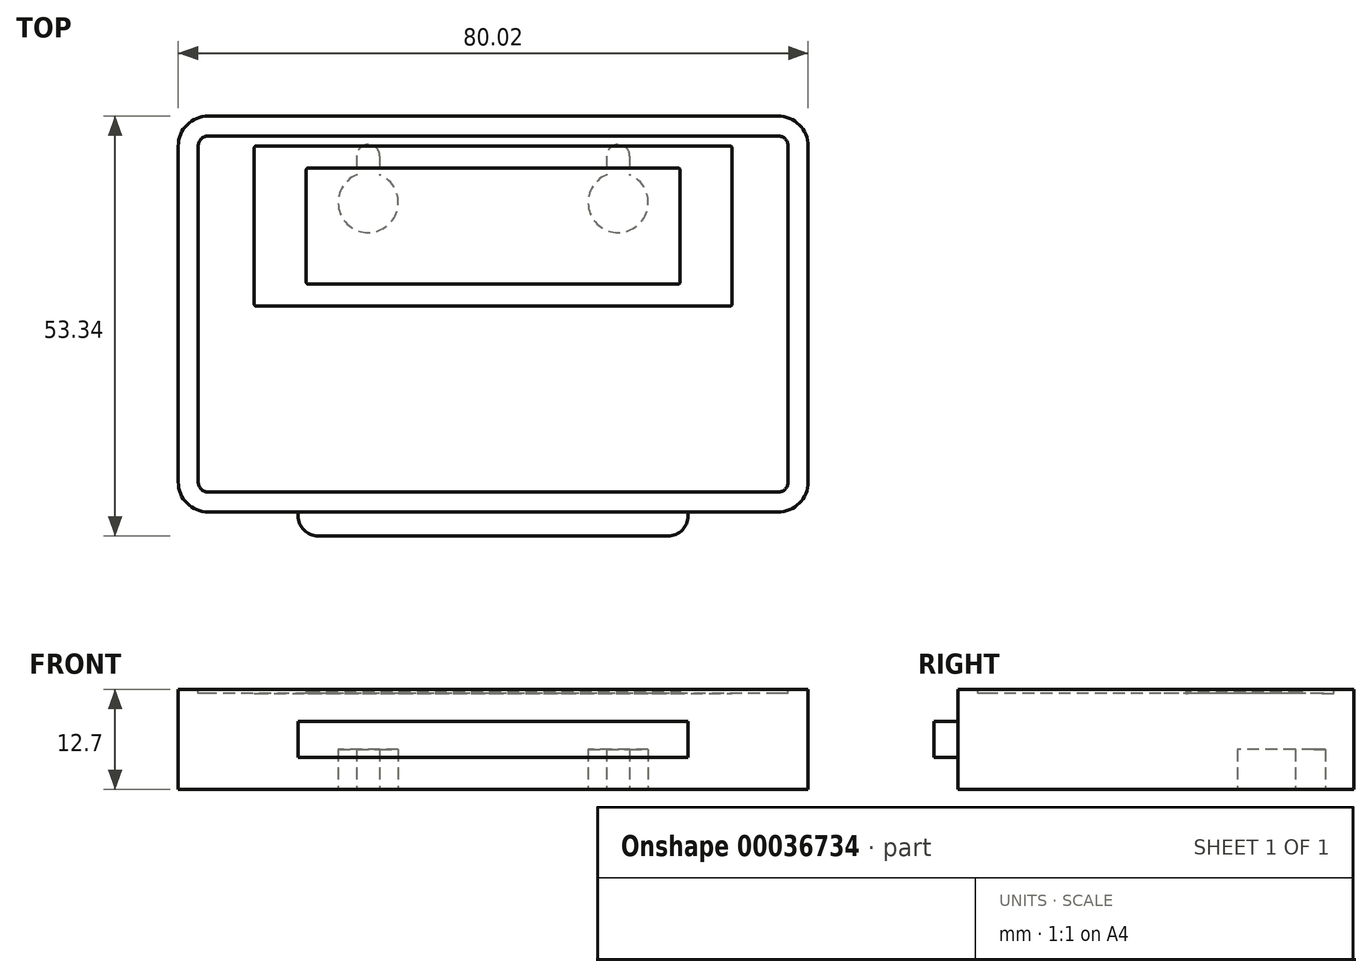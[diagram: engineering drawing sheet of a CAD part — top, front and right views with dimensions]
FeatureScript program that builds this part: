
annotation { "Feature Type Name" : "Feature", "Feature Type Description" : "" }
export const myFeature = defineFeature(function(context is Context, id is Id, definition is map)
    precondition{}
    {
        {
            var Q0;
            Q0=qCreatedBy(makeId("Top.planeOp"),FACE);
            var sketch = newSketch(context, id + "F0", { "sketchPlane" : qUnion([Q0])});
            skLineSegment(sketch, "E0.rect.bottom", {"start": v(40, 25.15) * mm, "end": v(-40, 25.15) * mm});
            skLineSegment(sketch, "E0.rect.top", {"start": v(40, -25.15) * mm, "end": v(-40, -25.15) * mm});
            skLineSegment(sketch, "E0.rect.left", {"start": v(40, 25.15) * mm, "end": v(40, -25.15) * mm});
            skLineSegment(sketch, "E0.rect.right", {"start": v(-40, 25.15) * mm, "end": v(-40, -25.15) * mm});
            skPoint(sketch, "E0.rect.middle", {"position": v(0, 0) * mm});
            skSolve(sketch);
        }
        {
            var Q0;
            Q0=makeQuery(id+"F0.imprint","IMPRINT",FACE,{"disambiguationData":[TD([[makeQuery(id+"F0.imprint","IMPRINT",EDGE,{"derivedFrom":sQuery(id+"F0.wireOp",EDGE,"E0.rect.bottom")}),1.0]])]});
            extrude(context, id + "F1", {"entities" : qUnion([Q0]), "endBound" : BoundingType.SYMMETRIC, "depth" : 12.7 * mm});
        }
        {
            var Q0;
            Q0=makeQuery(id+"F1.opExtrude","SWEPT_EDGE",EDGE,{"disambiguationData":[OSD([sQuery(id+"F0.wireOp",EDGE,"E0.rect.top"),sQuery(id+"F0.wireOp",EDGE,"E0.rect.right")])]});
            var Q1;
            Q1=makeQuery(id+"F1.opExtrude","SWEPT_EDGE",EDGE,{"disambiguationData":[OSD([sQuery(id+"F0.wireOp",EDGE,"E0.rect.top"),sQuery(id+"F0.wireOp",EDGE,"E0.rect.left")])]});
            var Q2;
            Q2=makeQuery(id+"F1.opExtrude","SWEPT_EDGE",EDGE,{"disambiguationData":[OSD([sQuery(id+"F0.wireOp",EDGE,"E0.rect.bottom"),sQuery(id+"F0.wireOp",EDGE,"E0.rect.left")])]});
            var Q3;
            Q3=makeQuery(id+"F1.opExtrude","SWEPT_EDGE",EDGE,{"disambiguationData":[OSD([sQuery(id+"F0.wireOp",EDGE,"E0.rect.bottom"),sQuery(id+"F0.wireOp",EDGE,"E0.rect.right")])]});
            fillet(context, id + "F2", {"entities" : qUnion([Q0, Q1, Q2, Q3]), "radius" : 3.8 * mm, "tangentPropagation" : true, "allowEdgeOverflow" : false});
        }
        {
            var Q0;
            Q0=makeQuery(id+"F1.opExtrude","CAP_FACE",FACE,{"disambiguationData":[OSD([sQuery(id+"F0.wireOp",EDGE,"E0.rect.bottom"),sQuery(id+"F0.wireOp",EDGE,"E0.rect.top"),sQuery(id+"F0.wireOp",EDGE,"E0.rect.left"),sQuery(id+"F0.wireOp",EDGE,"E0.rect.right")])],"isStart":false});
            var sketch = newSketch(context, id + "F3", { "sketchPlane" : qUnion([Q0])});
            skLineSegment(sketch, "E1.0", {"start": v(36.2, 22.62) * mm, "end": v(-36.2, 22.62) * mm});
            skArc(sketch, "E1.1", {"start": v(37.47, 21.34) * mm, "mid": v(37.1, 22.24) * mm, "end": v(36.2, 22.62) * mm});
            skLineSegment(sketch, "E1.2", {"start": v(37.47, 21.34) * mm, "end": v(37.47, -21.34) * mm});
            skArc(sketch, "E1.3", {"start": v(36.2, -22.62) * mm, "mid": v(37.1, -22.24) * mm, "end": v(37.47, -21.34) * mm});
            skLineSegment(sketch, "E1.4", {"start": v(36.2, -22.62) * mm, "end": v(-36.2, -22.62) * mm});
            skArc(sketch, "E1.5", {"start": v(-36.2, 22.62) * mm, "mid": v(-37.1, 22.24) * mm, "end": v(-37.47, 21.34) * mm});
            skArc(sketch, "E1.6", {"start": v(-37.47, -21.34) * mm, "mid": v(-37.1, -22.24) * mm, "end": v(-36.2, -22.62) * mm});
            skLineSegment(sketch, "E1.7", {"start": v(-37.47, 21.34) * mm, "end": v(-37.47, -21.34) * mm});
            skSolve(sketch);
        }
        {
            var Q0;
            Q0 = qSketchRegion(id + "F3", true);
            extrude(context, id + "F4", {"entities" : qUnion([Q0]), "operationType" : NewBodyOperationType.REMOVE, "oppositeDirection" : true, "depth" : 0.5 * mm});
        }
        {
            var Q0;
            Q0=makeQuery(id+"F1.opExtrude","SWEPT_FACE",FACE,{"disambiguationData":[OSD([sQuery(id+"F0.wireOp",EDGE,"E0.rect.top")])]});
            var sketch = newSketch(context, id + "F5", { "sketchPlane" : qUnion([Q0])});
            skLineSegment(sketch, "E2.bottom", {"start": v(-24.76, 2.29) * mm, "end": v(24.77, 2.29) * mm});
            skLineSegment(sketch, "E2.top", {"start": v(-24.76, -2.29) * mm, "end": v(24.77, -2.29) * mm});
            skLineSegment(sketch, "E2.left", {"start": v(-24.76, 2.29) * mm, "end": v(-24.76, -2.29) * mm});
            skLineSegment(sketch, "E2.right", {"start": v(24.77, 2.29) * mm, "end": v(24.77, -2.29) * mm});
            skSolve(sketch);
        }
        {
            var Q0;
            Q0=makeQuery(id+"F5.imprint","IMPRINT",FACE,{"disambiguationData":[TD([[makeQuery(id+"F5.imprint","IMPRINT",EDGE,{"derivedFrom":sQuery(id+"F5.wireOp",EDGE,"E2.bottom")}),-1.0]])]});
            extrude(context, id + "F6", {"entities" : qUnion([Q0]), "operationType" : NewBodyOperationType.ADD, "depth" : 3.05 * mm});
        }
        {
            var Q0;
            Q0=makeQuery(id+"F6.opExtrude","CAP_EDGE",EDGE,{"disambiguationData":[OSD([sQuery(id+"F5.wireOp",EDGE,"E2.right")])],"isStart":false});
            var Q1;
            Q1=makeQuery(id+"F6.opExtrude","CAP_EDGE",EDGE,{"disambiguationData":[OSD([sQuery(id+"F5.wireOp",EDGE,"E2.left")])],"isStart":false});
            fillet(context, id + "F7", {"entities" : qUnion([Q0, Q1]), "radius" : 2.54 * mm, "tangentPropagation" : true, "allowEdgeOverflow" : false});
        }
        {
            var Q0;
            Q0=makeQuery(id+"F4.boolean.opBoolean","COPY",FACE,{"derivedFrom":makeQuery(id+"F4.opExtrude","CAP_FACE",FACE,{"disambiguationData":[OSD([sQuery(id+"F3.wireOp",EDGE,"E1.0"),sQuery(id+"F3.wireOp",EDGE,"E1.1"),sQuery(id+"F3.wireOp",EDGE,"E1.2"),sQuery(id+"F3.wireOp",EDGE,"E1.3"),sQuery(id+"F3.wireOp",EDGE,"E1.4"),sQuery(id+"F3.wireOp",EDGE,"E1.5"),sQuery(id+"F3.wireOp",EDGE,"E1.6"),sQuery(id+"F3.wireOp",EDGE,"E1.7")])],"isStart":false})});
            var sketch = newSketch(context, id + "F8", { "sketchPlane" : qUnion([Q0])});
            skLineSegment(sketch, "E3.bottom", {"start": v(-30.1, 21.34) * mm, "end": v(30.1, 21.34) * mm});
            skLineSegment(sketch, "E3.top", {"start": v(-30.1, 1.02) * mm, "end": v(30.1, 1.02) * mm});
            skLineSegment(sketch, "E3.left", {"start": v(-30.35, 21.08) * mm, "end": v(-30.35, 1.27) * mm});
            skLineSegment(sketch, "E3.right", {"start": v(30.35, 21.08) * mm, "end": v(30.35, 1.27) * mm});
            skPoint(sketch, "E4.visualSharp", {"position": v(-30.35, 21.34) * mm});
            skArc(sketch, "E4.filletArc", {"start": v(-30.1, 21.34) * mm, "mid": v(-30.28, 21.26) * mm, "end": v(-30.35, 21.08) * mm});
            skPoint(sketch, "E5.visualSharp", {"position": v(-30.35, 1.02) * mm});
            skArc(sketch, "E5.filletArc", {"start": v(-30.35, 1.27) * mm, "mid": v(-30.28, 1.1) * mm, "end": v(-30.1, 1.02) * mm});
            skPoint(sketch, "E6.visualSharp", {"position": v(30.35, 1.02) * mm});
            skArc(sketch, "E6.filletArc", {"start": v(30.1, 1.02) * mm, "mid": v(30.28, 1.1) * mm, "end": v(30.35, 1.27) * mm});
            skPoint(sketch, "E7.visualSharp", {"position": v(30.35, 21.34) * mm});
            skArc(sketch, "E7.filletArc", {"start": v(30.35, 21.08) * mm, "mid": v(30.28, 21.26) * mm, "end": v(30.1, 21.34) * mm});
            skSolve(sketch);
        }
        {
            var Q0;
            Q0=makeQuery(id+"F8.imprint","IMPRINT",FACE,{"disambiguationData":[TD([[makeQuery(id+"F8.imprint","IMPRINT",EDGE,{"derivedFrom":sQuery(id+"F8.wireOp",EDGE,"E3.bottom")}),-1.0]])]});
            extrude(context, id + "F9", {"entities" : qUnion([Q0]), "operationType" : NewBodyOperationType.ADD, "depth" : 0.03 * mm});
        }
        {
            var Q0;
            Q0=makeQuery(id+"F9.opExtrude","CAP_FACE",FACE,{"disambiguationData":[OSD([sQuery(id+"F8.wireOp",EDGE,"E3.bottom"),sQuery(id+"F8.wireOp",EDGE,"E3.top"),sQuery(id+"F8.wireOp",EDGE,"E3.left"),sQuery(id+"F8.wireOp",EDGE,"E3.right"),sQuery(id+"F8.wireOp",EDGE,"E4.filletArc"),sQuery(id+"F8.wireOp",EDGE,"E5.filletArc"),sQuery(id+"F8.wireOp",EDGE,"E6.filletArc"),sQuery(id+"F8.wireOp",EDGE,"E7.filletArc")])],"isStart":false});
            var sketch = newSketch(context, id + "F10", { "sketchPlane" : qUnion([Q0])});
            skLineSegment(sketch, "E8.bottom", {"start": v(-23.5, 18.54) * mm, "end": v(23.5, 18.54) * mm});
            skLineSegment(sketch, "E8.top", {"start": v(-23.5, 3.81) * mm, "end": v(23.5, 3.81) * mm});
            skLineSegment(sketch, "E8.left", {"start": v(-23.75, 18.29) * mm, "end": v(-23.75, 4.06) * mm});
            skLineSegment(sketch, "E8.right", {"start": v(23.75, 18.29) * mm, "end": v(23.75, 4.06) * mm});
            skPoint(sketch, "E9.visualSharp", {"position": v(-23.75, 18.54) * mm});
            skArc(sketch, "E9.filletArc", {"start": v(-23.5, 18.54) * mm, "mid": v(-23.67, 18.47) * mm, "end": v(-23.75, 18.29) * mm});
            skPoint(sketch, "E10.visualSharp", {"position": v(-23.75, 3.81) * mm});
            skArc(sketch, "E10.filletArc", {"start": v(-23.75, 4.06) * mm, "mid": v(-23.67, 3.88) * mm, "end": v(-23.5, 3.81) * mm});
            skPoint(sketch, "E11.visualSharp", {"position": v(23.75, 3.81) * mm});
            skArc(sketch, "E11.filletArc", {"start": v(23.5, 3.81) * mm, "mid": v(23.67, 3.88) * mm, "end": v(23.75, 4.06) * mm});
            skPoint(sketch, "E12.visualSharp", {"position": v(23.75, 18.54) * mm});
            skArc(sketch, "E12.filletArc", {"start": v(23.75, 18.29) * mm, "mid": v(23.67, 18.47) * mm, "end": v(23.5, 18.54) * mm});
            skSolve(sketch);
        }
        {
            var Q0;
            Q0=makeQuery(id+"F10.imprint","IMPRINT",FACE,{"disambiguationData":[TD([[makeQuery(id+"F10.imprint","IMPRINT",EDGE,{"derivedFrom":sQuery(id+"F10.wireOp",EDGE,"E8.bottom")}),-1.0]])]});
            extrude(context, id + "F11", {"entities" : qUnion([Q0]), "operationType" : NewBodyOperationType.ADD, "depth" : 0.25 * mm});
        }
        {
            var Q0;
            Q0=makeQuery(id+"F1.opExtrude","CAP_FACE",FACE,{"disambiguationData":[OSD([sQuery(id+"F0.wireOp",EDGE,"E0.rect.bottom"),sQuery(id+"F0.wireOp",EDGE,"E0.rect.top"),sQuery(id+"F0.wireOp",EDGE,"E0.rect.left"),sQuery(id+"F0.wireOp",EDGE,"E0.rect.right")])],"isStart":true});
            var sketch = newSketch(context, id + "F12", { "sketchPlane" : qUnion([Q0])});
            skArc(sketch, "E13", {"start": v(14.4, -20.05) * mm, "mid": v(15.87, -21.54) * mm, "end": v(17.35, -20.07) * mm});
            skArc(sketch, "E14", {"start": v(17.35, -17.69) * mm, "mid": v(15.87, -10.36) * mm, "end": v(14.4, -17.69) * mm});
            skLineSegment(sketch, "E15", {"start": v(15.88, -20.07) * mm, "end": v(15.88, -14.17) * mm, "construction": true});
            skLineSegment(sketch, "E16", {"start": v(17.35, -20.07) * mm, "end": v(17.35, -17.69) * mm});
            skLineSegment(sketch, "E17", {"start": v(14.4, -20.08) * mm, "end": v(14.4, -17.69) * mm});
            skArc(sketch, "E18.MirrorCS", {"start": v(-17.35, -17.69) * mm, "mid": v(-15.87, -10.36) * mm, "end": v(-14.4, -17.69) * mm});
            skLineSegment(sketch, "E19.MirrorCS", {"start": v(-17.35, -20.07) * mm, "end": v(-17.35, -17.69) * mm});
            skArc(sketch, "E20.MirrorCS", {"start": v(-14.4, -20.05) * mm, "mid": v(-15.87, -21.54) * mm, "end": v(-17.35, -20.07) * mm});
            skLineSegment(sketch, "E21.MirrorCS", {"start": v(-14.4, -20.08) * mm, "end": v(-14.4, -17.69) * mm});
            skSolve(sketch);
        }
        {
            var Q0;
            Q0 = qSketchRegion(id + "F12", true);
            extrude(context, id + "F13", {"entities" : qUnion([Q0]), "operationType" : NewBodyOperationType.REMOVE, "oppositeDirection" : true, "depth" : 5.08 * mm});
        }
    });
